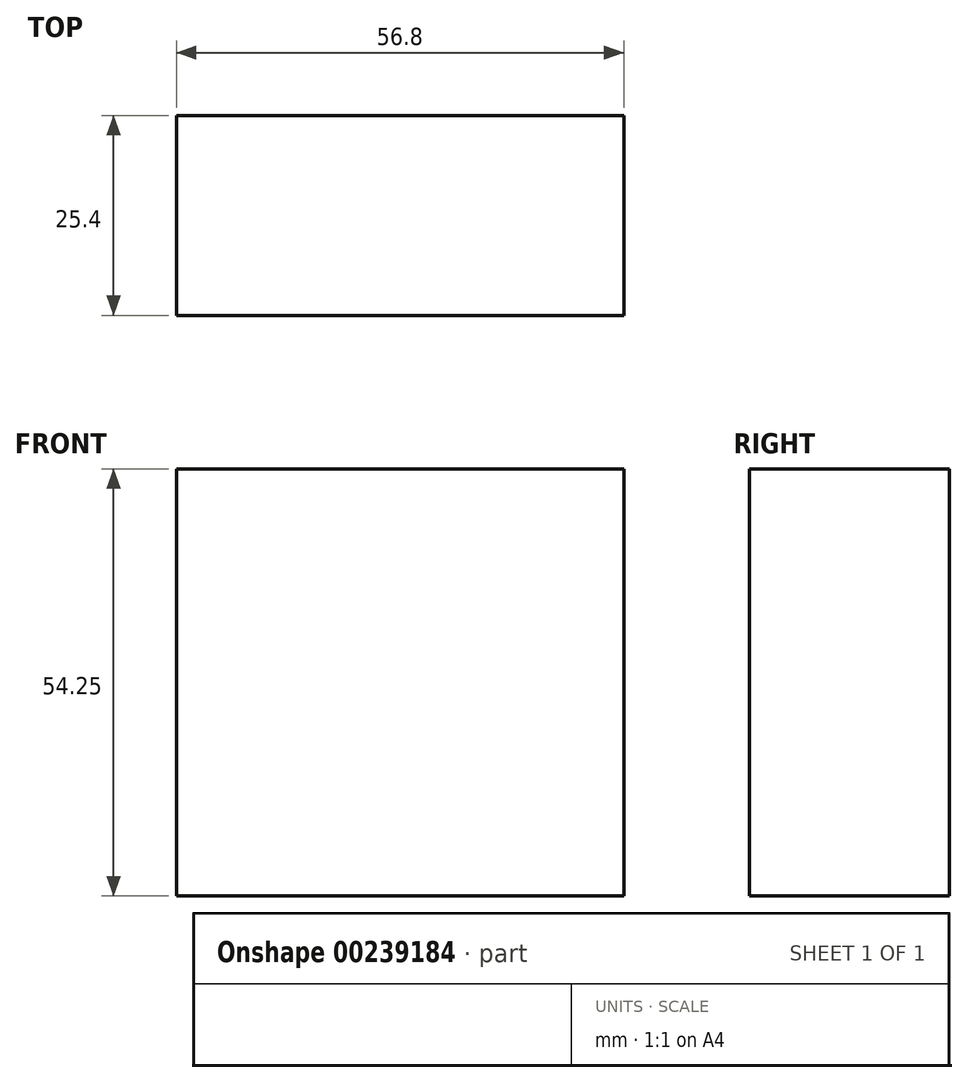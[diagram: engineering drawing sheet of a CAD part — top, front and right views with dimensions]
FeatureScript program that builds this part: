
annotation { "Feature Type Name" : "Feature", "Feature Type Description" : "" }
export const myFeature = defineFeature(function(context is Context, id is Id, definition is map)
    precondition{}
    {
        {
            var Q0;
            Q0=qCreatedBy(makeId("Front.planeOp"),FACE);
            var sketch = newSketch(context, id + "F0", { "sketchPlane" : qUnion([Q0])});
            skLineSegment(sketch, "E0.bottom", {"start": v(-27.03, 17.33) * mm, "end": v(29.77, 17.33) * mm});
            skLineSegment(sketch, "E0.top", {"start": v(-27.03, -36.92) * mm, "end": v(29.77, -36.92) * mm});
            skLineSegment(sketch, "E0.left", {"start": v(-27.03, 17.33) * mm, "end": v(-27.03, -36.92) * mm});
            skLineSegment(sketch, "E0.right", {"start": v(29.77, 17.33) * mm, "end": v(29.77, -36.92) * mm});
            skSolve(sketch);
        }
        {
            var Q0;
            Q0 = qSketchRegion(id + "F0", true);
            extrude(context, id + "F1", {"entities" : qUnion([Q0]), "endBound" : BoundingType.SYMMETRIC, "depth" : 25.4 * mm});
        }
    });
